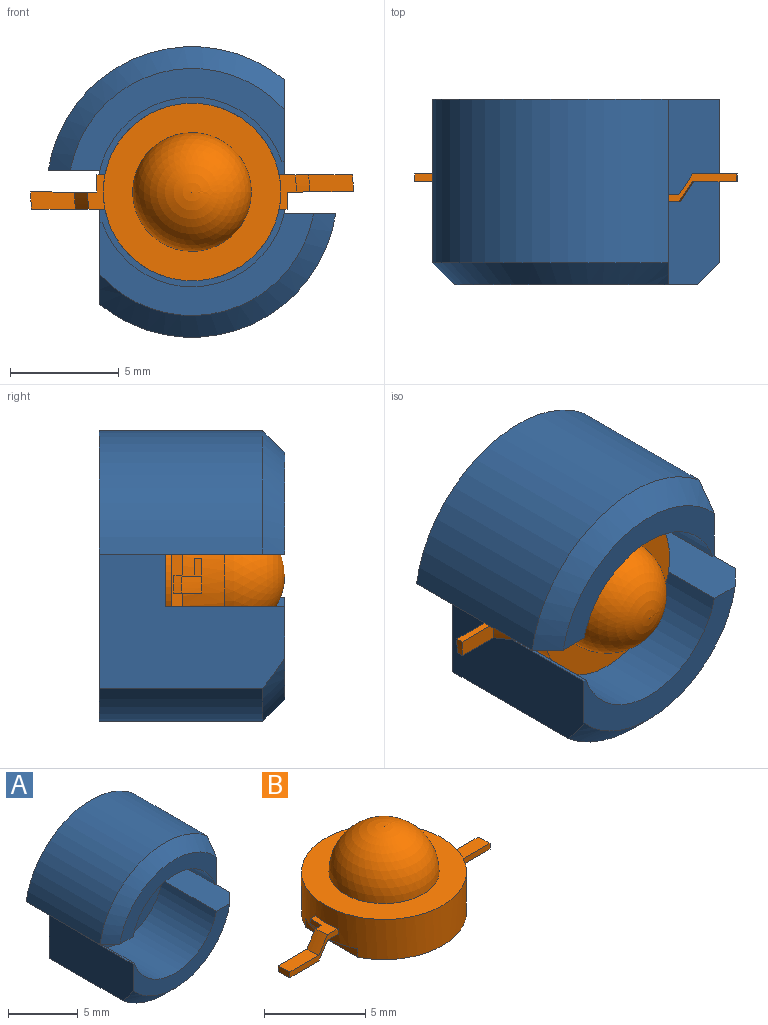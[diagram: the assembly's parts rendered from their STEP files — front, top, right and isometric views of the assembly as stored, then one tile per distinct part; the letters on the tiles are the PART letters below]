
ASSEMBLY  parts=2 mates=1
PART A: 17 faces, bbox 13.2x8.5x13.3 mm
  f0: cylinder r=6.67mm len=10.83mm, axis (0,1,0), area 105.4mm2, adj f2,f7,f10,f14
  f1: plane 9.81x4.67mm, normal (0,-1,0), area 15.8mm2, adj f6,f7,f10,f13,f14
  f2: plane 13.34x13.18mm, normal (0,1,0), area 113.4mm2, adj f0,f5,f7,f9,f10,f11,f16
  f3: plane 8.7x8.47mm, normal (0,-1,0), area 55.2mm2, adj f6,f8,f10,f11,f12,f13,f16
  f4: plane 9.81x4.67mm, normal (0,-1,0), area 15.8mm2, adj f8,f9,f11,f12,f15
  f5: cylinder r=6.67mm len=10.83mm, axis (0,1,0), area 105.4mm2, adj f2,f9,f11,f15
  f6: cylinder r=4.35mm len=8.35mm, axis (0,-1,0), area 61.6mm2, adj f1,f3,f7,f13
  f7: plane 8.51x2.37mm, normal (0,0,1), area 19.5mm2, adj f0,f1,f2,f6,f11,f14
  f8: cylinder r=4.35mm len=8.35mm, axis (0,-1,0), area 61.6mm2, adj f3,f4,f9,f12
  f9: plane 8.51x2.37mm, normal (0,0,-1), area 19.5mm2, adj f2,f4,f5,f8,f10,f15
  f10: plane 8.5x6.15mm, normal (-1,0,0), area 38.4mm2, adj f0,f1,f2,f3,f9,f13,f14
  f11: plane 8.5x6.15mm, normal (1,0,0), area 38.4mm2, adj f2,f3,f4,f5,f7,f12,f15
  f12: plane 5.48x0.11mm, normal (0.16,0,-0.99), area 0.6mm2, adj f3,f4,f8,f11
  f13: plane 5.48x0.11mm, normal (-0.16,0,0.99), area 0.6mm2, adj f1,f3,f6,f10
  f14: cone r=5.67mm half-angle=45deg, axis (0,1,0), area 18.9mm2, adj f0,f1,f7,f10
  f15: cone r=5.67mm half-angle=45deg, axis (0,1,0), area 18.9mm2, adj f4,f5,f9,f11
  f16: cylinder r=1.13mm len=3.02mm, axis (0,1,0), area 21.4mm2, adj f2,f3
PART B: 32 faces, bbox 14.8x8.2x5.5 mm
  f0: cone r=4.79mm half-angle=32.7deg, axis (0,0,-1), area 0.9mm2, adj f1,f5,f26,f30
  f1: plane 2.06x0.79mm, normal (0,0,-1), area 1.6mm2, adj f0,f13,f26,f30
  f2: plane 2.06x0.79mm, normal (0,0,1), area 1.6mm2, adj f3,f13,f26,f30
  f3: cone r=4.79mm half-angle=33.3deg, axis (0,0,-1), area 0.9mm2, adj f2,f4,f26,f30
  f4: plane 1.58x0.79mm, normal (0,0,1), area 0.8mm2, adj f3,f12,f20,f26,f30,f31
  f5: plane 1.58x0.79mm, normal (0,0,-1), area 0.8mm2, adj f0,f12,f20,f26,f30,f31
  f6: cone r=4.79mm half-angle=32.7deg, axis (0,0,-1), area 0.9mm2, adj f7,f11,f25,f28
  f7: plane 2.06x0.79mm, normal (0,0,-1), area 1.6mm2, adj f6,f14,f25,f28
  f8: plane 2.06x0.79mm, normal (0,0,1), area 1.6mm2, adj f9,f14,f25,f28
  f9: cone r=4.79mm half-angle=33.3deg, axis (0,0,-1), area 0.9mm2, adj f8,f10,f25,f28
  f10: plane 1.58x0.79mm, normal (0,0,1), area 0.8mm2, adj f9,f20,f25,f27,f28,f29
  f11: plane 1.58x0.79mm, normal (0,0,-1), area 0.8mm2, adj f6,f20,f25,f27,f28,f29
  f12: plane 0.36x0.33mm, normal (0,-1,0), area 0.1mm2, adj f4,f5,f20,f31
  f13: cylinder r=7.4mm len=0.79mm, axis (0,0,1), area 0.3mm2, adj f1,f2,f26,f30
  f14: cylinder r=7.4mm len=0.79mm, axis (0,0,1), area 0.3mm2, adj f7,f8,f25,f28
  f15: plane 8.15x7.3mm, normal (0,0,-1), area 26.8mm2, adj f19,f20,f21,f23
  f16: plane 8.15x8.15mm, normal (0,0,1), area 28.9mm2, adj f17,f20
  f17: sphere r=2.72mm, area 47mm2, adj f16
  f18: plane 5.45x5.45mm, normal (0,0,-1), area 23.3mm2, adj f19
  f19: cylinder r=2.73mm len=5.45mm, axis (0,0,1), area 5.1mm2, adj f15,f18
  f20: cylinder r=4.07mm len=8.15mm, axis (0,0,1), area 57.4mm2, adj f4,f5,f10,f11,f12,f15,f16,f21
  f21: plane 3.62x0.5mm, normal (1,0,0), area 1.8mm2, adj f15,f20,f22
  f22: plane 3.62x0.42mm, normal (0,0,-1), area 1mm2, adj f20,f21
  f23: plane 3.62x0.5mm, normal (-1,0,0), area 1.8mm2, adj f15,f20,f24
  f24: plane 3.62x0.42mm, normal (0,0,-1), area 1mm2, adj f20,f23
  f25: plane 3.37x1.29mm, normal (0,-1,0), area 1.2mm2, adj f6,f7,f8,f9,f10,f11,f14,f20
  f26: plane 3.37x1.29mm, normal (0,1,0), area 1.2mm2, adj f0,f1,f2,f3,f4,f5,f13,f20
  f27: plane 0.36x0.33mm, normal (0,1,0), area 0.1mm2, adj f10,f11,f20,f29
  f28: plane 3.04x1.28mm, normal (0,1,0), area 1mm2, adj f6,f7,f8,f9,f10,f11,f14,f29
  f29: plane 0.79x0.33mm, normal (-1,0,0), area 0.3mm2, adj f10,f11,f27,f28
  f30: plane 3.04x1.28mm, normal (0,-1,0), area 1mm2, adj f0,f1,f2,f3,f4,f5,f13,f31
  f31: plane 0.79x0.33mm, normal (1,0,0), area 0.3mm2, adj f4,f5,f12,f30
PLACE A t=(-1.5,2.07,-1.97)mm fixed
PLACE B rot(axis=(1,0,0),90deg) t=(-1.5,-0.95,-1.97)mm
MATE fastened B.f0 <-> A.f8  axis (0,1,0) through (-1.5,-0.95,-1.97)mm
